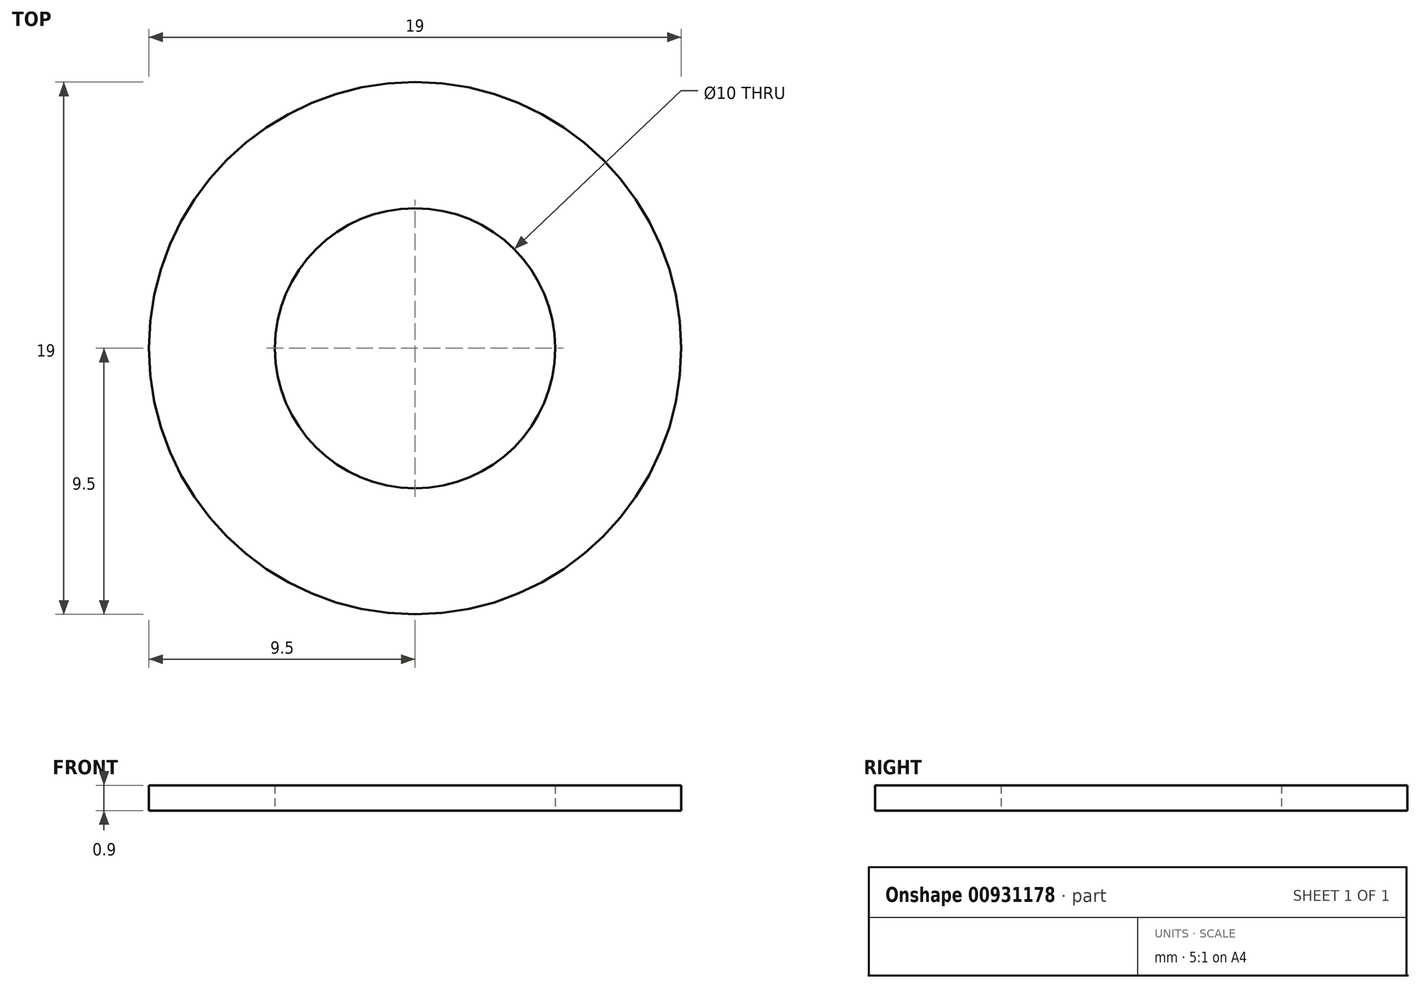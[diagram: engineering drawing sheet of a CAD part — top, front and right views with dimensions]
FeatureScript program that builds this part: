
annotation { "Feature Type Name" : "Feature", "Feature Type Description" : "" }
export const myFeature = defineFeature(function(context is Context, id is Id, definition is map)
    precondition{}
    {
        {
            var Q0;
            Q0=qCreatedBy(makeId("Top.planeOp"),FACE);
            var sketch = newSketch(context, id + "F0", { "sketchPlane" : qUnion([Q0])});
            skCircle(sketch, "E0", {"center": v(0, 0) * mm, "radius": 9.5 * mm});
            skCircle(sketch, "E1", {"center": v(0, 0) * mm, "radius": 5 * mm});
            skSolve(sketch);
        }
        {
            var Q0;
            Q0=makeQuery(id+"F0.imprint","IMPRINT",FACE,{"disambiguationData":[TD([[makeQuery(id+"F0.imprint","IMPRINT",EDGE,{"derivedFrom":sQuery(id+"F0.wireOp",EDGE,"E0")}),1.0]])]});
            extrude(context, id + "F1", {"entities" : qUnion([Q0]), "depth" : 0.9 * mm, "offsetDistance" : 25 * mm});
        }
    });
